# Revit family: Highstreet
name_source: partatom
category: Furniture
revit_build: Autodesk Revit 2016 (Build: 20151209_0715(x64)
units: mm (PartAtom-declared; Revit-internal decimal feet)

## family parameters
Always vertical = Yes
Cut with Voids When Loaded = No
OmniClass Number = 23.40.20.00
OmniClass Title = General Furniture and Specialties
Room Calculation Point = No
Shared = No
Work Plane-Based = No

## types (5) — shared parameters
Depth = 34"
Seat Height = 20"

## per-type parameters (varying)
| type | Base | Chair Back | Cushion 2 | Cushion 3 | Cushion Width | Furniture Geometry | Loveseat Back | Ottoman Feet | Seat Depth | Seat Width | Slide Out Ottoman | Sofa Back |
| Chair | Yes | Yes | No | No | 22" | Yes | No | No | 22" | 22" | No | No |
| Sofa | Yes | No | Yes | Yes | 22" | Yes | No | No | 22" | 66" | No | Yes |
| Loveseat | Yes | No | Yes | No | 22" | Yes | Yes | No | 22" | 44" | No | No |
| Chair-Slide Out Ottoman | No | Yes | No | No | 22" | Yes | No | No | 22" | 22" | Yes | No |
| Ottoman | Yes | No | No | No | 28 1/2" | No | No | Yes | 22 1/2" | 28 1/2" | No | No |

## geometry (parser evidence)
native form markers: Sweep x44
no freeform markers — native parametric forms only
